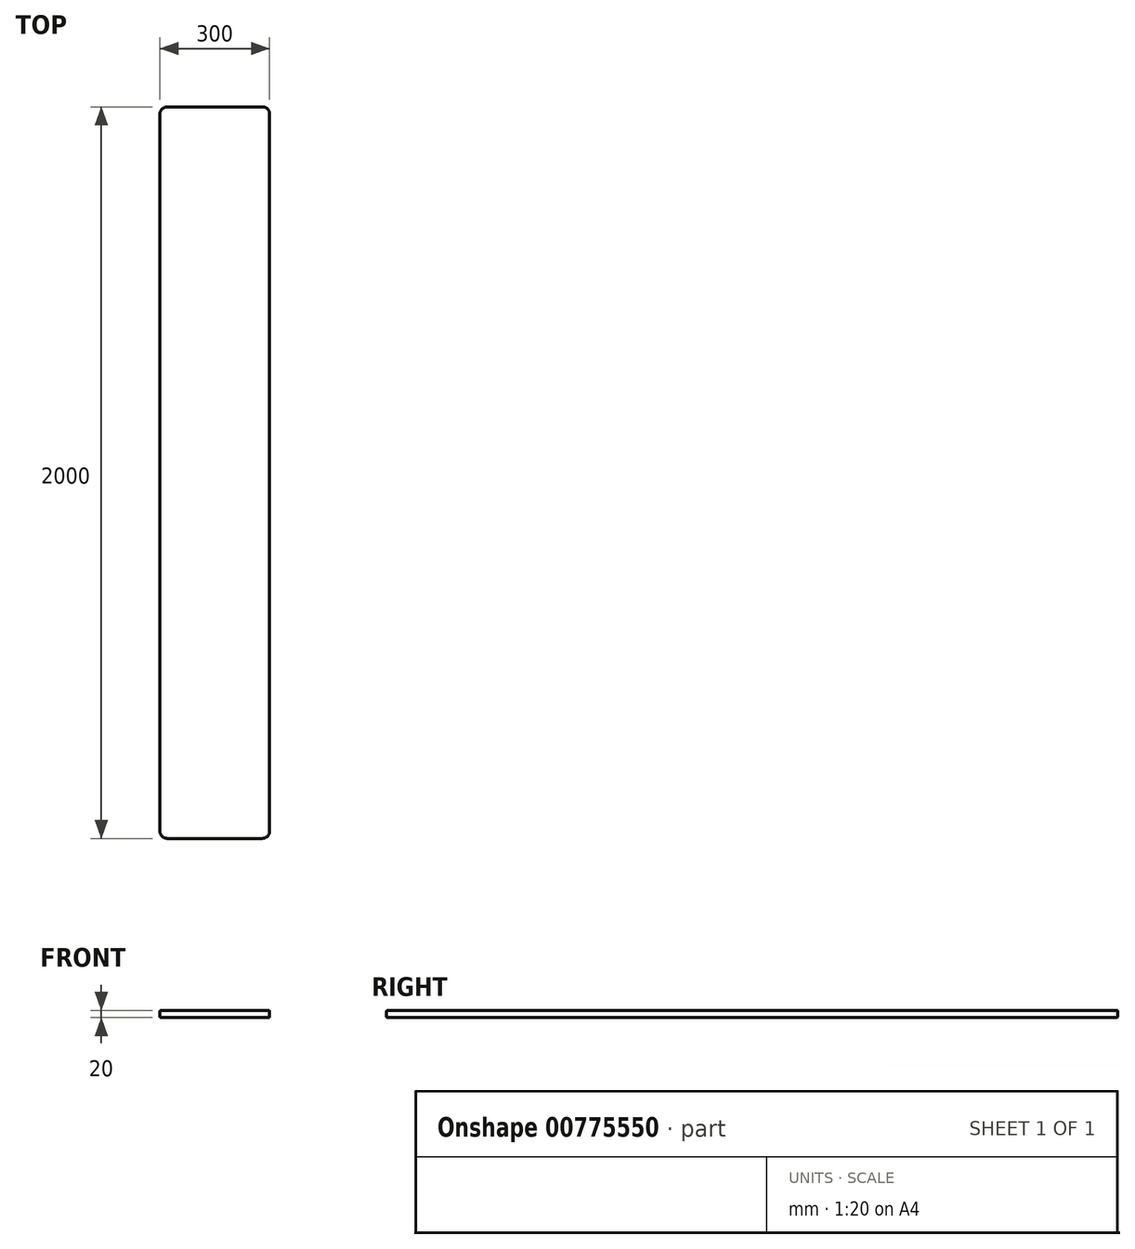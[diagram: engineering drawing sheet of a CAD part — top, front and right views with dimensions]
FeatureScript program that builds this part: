
annotation { "Feature Type Name" : "Feature", "Feature Type Description" : "" }
export const myFeature = defineFeature(function(context is Context, id is Id, definition is map)
    precondition{}
    {
        {
            var Q0;
            Q0=qCreatedBy(makeId("Front.planeOp"),FACE);
            var sketch = newSketch(context, id + "F0", { "sketchPlane" : qUnion([Q0])});
            skLineSegment(sketch, "E0.bottom", {"start": v(-83.95, 0) * mm, "end": v(216.05, 0) * mm});
            skLineSegment(sketch, "E0.top", {"start": v(-83.95, 20) * mm, "end": v(216.05, 20) * mm});
            skLineSegment(sketch, "E0.left", {"start": v(-83.95, 0) * mm, "end": v(-83.95, 20) * mm});
            skLineSegment(sketch, "E0.right", {"start": v(216.05, 0) * mm, "end": v(216.05, 20) * mm});
            skSolve(sketch);
        }
        {
            var Q0;
            Q0=makeQuery(id+"F0.imprint","IMPRINT",FACE,{"disambiguationData":[TD([[makeQuery(id+"F0.imprint","IMPRINT",EDGE,{"derivedFrom":sQuery(id+"F0.wireOp",EDGE,"E0.bottom")}),1.0]])]});
            extrude(context, id + "F1", {"entities" : qUnion([Q0]), "depth" : 2000 * mm, "offsetDistance" : 25 * mm});
        }
        {
            var Q0;
            Q0=makeQuery(id+"F1.opExtrude","SWEPT_FACE",FACE,{"disambiguationData":[OSD([sQuery(id+"F0.wireOp",EDGE,"E0.top")])]});
            var Q1;
            Q1=makeQuery(id+"F1.opExtrude","SWEPT_FACE",FACE,{"disambiguationData":[OSD([sQuery(id+"F0.wireOp",EDGE,"E0.bottom")])]});
            fillet(context, id + "F2", {"entities" : qUnion([Q0, Q1]), "radius" : 3 * mm, "tangentPropagation" : true, "allowEdgeOverflow" : false});
        }
        {
            var Q0;
            Q0=makeQuery(id+"F1.opExtrude","CAP_EDGE",EDGE,{"disambiguationData":[OSD([sQuery(id+"F0.wireOp",EDGE,"E0.right")])],"isStart":true});
            var Q1;
            Q1=makeQuery(id+"F1.opExtrude","CAP_EDGE",EDGE,{"disambiguationData":[OSD([sQuery(id+"F0.wireOp",EDGE,"E0.left")])],"isStart":true});
            var Q2;
            Q2=makeQuery(id+"F1.opExtrude","CAP_EDGE",EDGE,{"disambiguationData":[OSD([sQuery(id+"F0.wireOp",EDGE,"E0.right")])],"isStart":false});
            var Q3;
            Q3=makeQuery(id+"F1.opExtrude","CAP_EDGE",EDGE,{"disambiguationData":[OSD([sQuery(id+"F0.wireOp",EDGE,"E0.left")])],"isStart":false});
            fillet(context, id + "F3", {"entities" : qUnion([Q0, Q1, Q2, Q3]), "radius" : 20 * mm, "tangentPropagation" : true, "allowEdgeOverflow" : false});
        }
        {
            var Q0;
            Q0=makeQuery(id+"F1.opExtrude","SWEPT_FACE",FACE,{"disambiguationData":[OSD([sQuery(id+"F0.wireOp",EDGE,"E0.top")])]});
            var sketch = newSketch(context, id + "F4", { "sketchPlane" : qUnion([Q0])});
            skLineSegment(sketch, "E1", {"start": v(166.05, 0) * mm, "end": v(166.05, -50) * mm, "construction": true});
            skLineSegment(sketch, "E2", {"start": v(166.05, -50) * mm, "end": v(216.05, -50) * mm, "construction": true});
            skLineSegment(sketch, "E3", {"start": v(166.05, -50) * mm, "end": v(166.05, -680) * mm, "construction": true});
            skLineSegment(sketch, "E4", {"start": v(166.05, -680) * mm, "end": v(166.05, -1320) * mm, "construction": true});
            skLineSegment(sketch, "E5", {"start": v(166.05, -1320) * mm, "end": v(166.05, -1950) * mm, "construction": true});
            skLineSegment(sketch, "E6", {"start": v(166.05, -1950) * mm, "end": v(166.05, -2000) * mm, "construction": true});
            skLineSegment(sketch, "E7", {"start": v(166.05, -1950) * mm, "end": v(-33.95, -1950) * mm, "construction": true});
            skLineSegment(sketch, "E8", {"start": v(166.05, -50) * mm, "end": v(-33.95, -50) * mm, "construction": true});
            skLineSegment(sketch, "E9", {"start": v(166.05, -680) * mm, "end": v(-33.95, -680) * mm, "construction": true});
            skLineSegment(sketch, "E10", {"start": v(166.05, -1320) * mm, "end": v(-33.95, -1320) * mm, "construction": true});
            skSolve(sketch);
        }
    });
